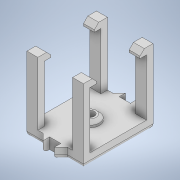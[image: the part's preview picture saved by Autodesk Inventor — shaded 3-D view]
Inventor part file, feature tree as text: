
AUTODESK INVENTOR PART (.ipt)
format: ipt  version: 2020.4 (Build 244396000, 396)  size: 225,792 bytes
history: native  units: in
note: dims shown in document units (in); Inventor stores cm internally (conversion verified against a paired STEP export)
features: extrude x7, sketch x7, chamfer x3, mirror x3, fillet x1
ambient origin geometry x8: Origin, YZ Plane, XZ Plane, XY Plane, X Axis, Y Axis, Z Axis, Center Point
bodies: Solid1 (feature_tree)
feature tree (21):
  extrude  "Extrusion1"  Depth=1.2598in
  extrude  "Extrusion2"  Depth=0.1969in
  extrude  "Extrusion3"  Depth=1.1417in TaperAngle=0.0deg
  chamfer  "Chamfer1"  Distance=0.1181in
  mirror  "Mirror1"
  mirror  "Mirror2"
  extrude  "Extrusion4"  Depth=0.0787in
  extrude  "Extrusion5"  Depth=0.7874in
  chamfer  "Chamfer2"  Distance=0.7874in
  extrude  "Extrusion15"  Depth=0.6299in
  extrude  "Extrusion16"  Depth=0.2362in
  chamfer  "Chamfer6"  Distance=0.0984in
  mirror  "Mirror4"
  fillet  "Fillet2"  Radius=0.1181in
  sketch  "Sketch1"  dims[d0=1.0236in d1=1.2598in]
  sketch  "Sketch2"  dims[d2=0.1969in d3=0.0in d4=0.1969in]
  sketch  "Sketch3"  dims[d5=0.1181in d6=1.1417in d7=0.0in]
  sketch  "Sketch4"  dims[d8=0.1181in d9=0.1181in d10=0.0in]
  sketch  "Sketch5"  dims[d11=0.0787in d12=0.0787in d13=45.0deg d14=0.3406in]
  sketch  "Sketch15"  dims[d15=0.0984in d16=0.0in d17=0.1575in d18=0.7874in d19=0.0in]
  sketch  "Sketch16"  dims[d20=0.0591in d21=0.0787in d22=45.0deg d66=0.6299in d67=0.2362in d68=0.0984in d69=0.0in d70=0.1181in d71=0.1181in d72=0.1181in d73=0.0in d74=0.1181in d75=0.0787in d76=45.0deg d77=0.0787in d24=0.0197in d25=0.0344in d26=0.0197in d27=0.0344in]
